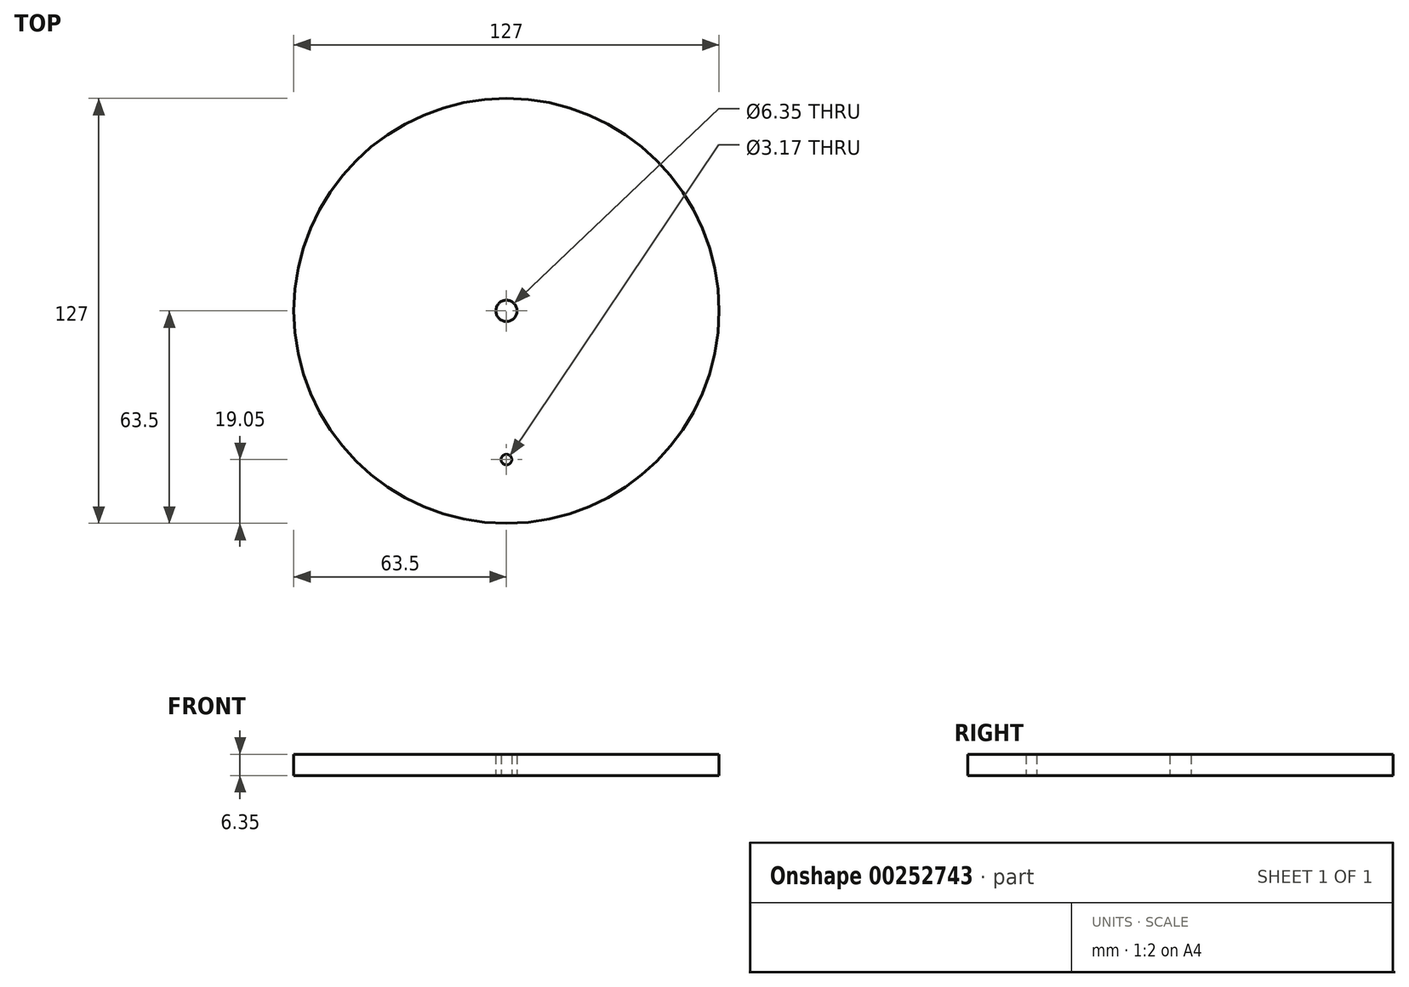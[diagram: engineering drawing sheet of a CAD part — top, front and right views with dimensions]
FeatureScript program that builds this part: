
annotation { "Feature Type Name" : "Feature", "Feature Type Description" : "" }
export const myFeature = defineFeature(function(context is Context, id is Id, definition is map)
    precondition{}
    {
        {
            var Q0;
            Q0=qCreatedBy(makeId("Top.planeOp"),FACE);
            var sketch = newSketch(context, id + "F0", { "sketchPlane" : qUnion([Q0])});
            skCircle(sketch, "E0", {"center": v(0, 0) * mm, "radius": 63.5 * mm});
            skCircle(sketch, "E1", {"center": v(0, 0) * mm, "radius": 3.18 * mm});
            skCircle(sketch, "E2", {"center": v(0, -44.45) * mm, "radius": 1.59 * mm});
            skSolve(sketch);
        }
        {
            var Q0;
            Q0 = qSketchRegion(id + "F0", true);
            extrude(context, id + "F1", {"entities" : qUnion([Q0]), "depth" : 6.35 * mm});
        }
    });
